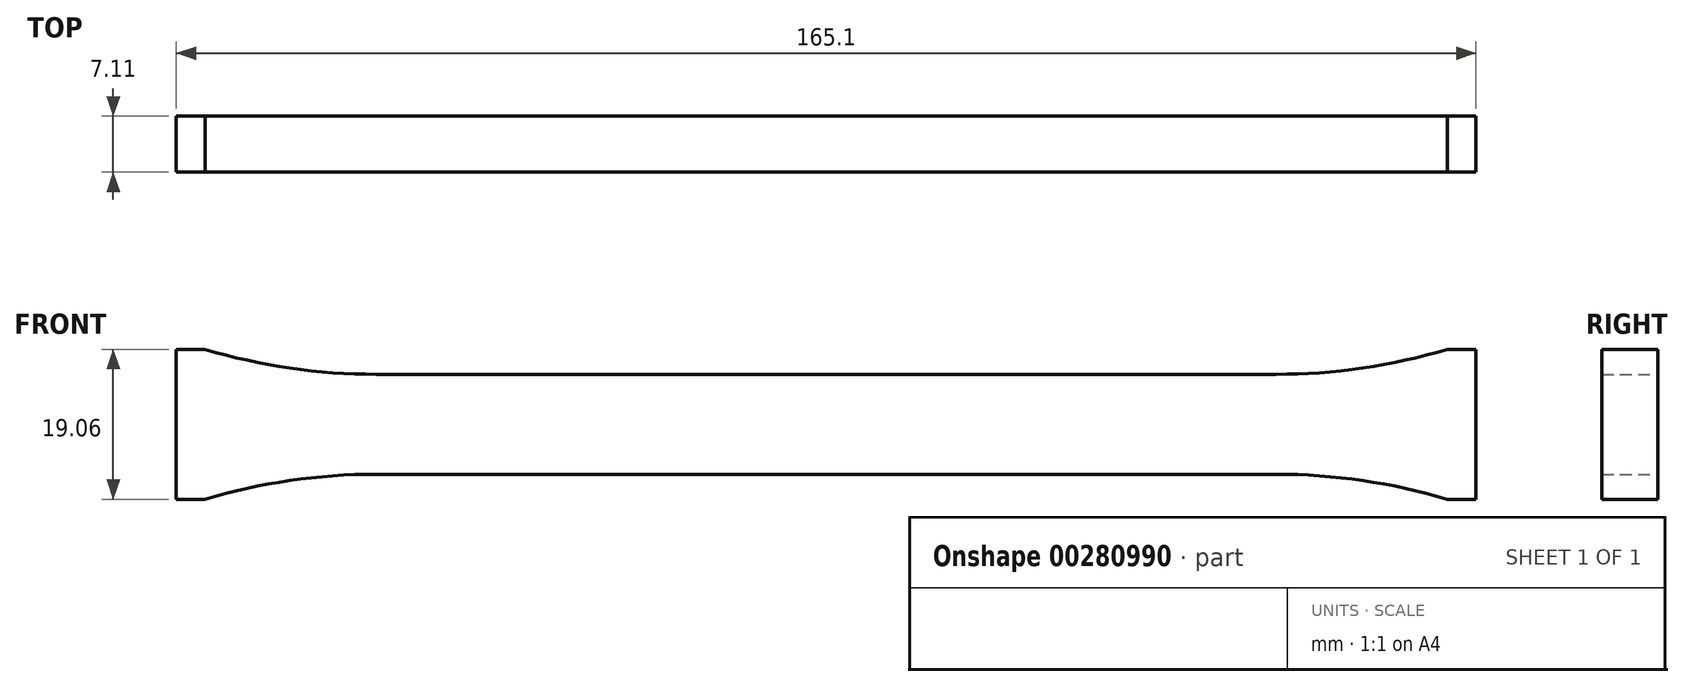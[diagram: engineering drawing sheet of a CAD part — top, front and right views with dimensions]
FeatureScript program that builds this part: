
annotation { "Feature Type Name" : "Feature", "Feature Type Description" : "" }
export const myFeature = defineFeature(function(context is Context, id is Id, definition is map)
    precondition{}
    {
        {
            var Q0;
            Q0=qCreatedBy(makeId("Front.planeOp"),FACE);
            var sketch = newSketch(context, id + "F0", { "sketchPlane" : qUnion([Q0])});
            skLineSegment(sketch, "E0", {"start": v(0, 6.35) * mm, "end": v(57.15, 6.35) * mm});
            skArc(sketch, "E1", {"start": v(57.15, 6.35) * mm, "mid": v(68.15, 7.15) * mm, "end": v(78.92, 9.53) * mm});
            skLineSegment(sketch, "E2", {"start": v(78.92, 9.53) * mm, "end": v(82.55, 9.53) * mm});
            skLineSegment(sketch, "E3", {"start": v(82.55, 9.52) * mm, "end": v(82.55, 0) * mm});
            skLineSegment(sketch, "E4.MirrorCS", {"start": v(82.55, -9.53) * mm, "end": v(82.55, 0) * mm});
            skLineSegment(sketch, "E5.MirrorCS", {"start": v(78.92, -9.53) * mm, "end": v(82.55, -9.53) * mm});
            skLineSegment(sketch, "E6.MirrorCS", {"start": v(0, -6.35) * mm, "end": v(57.15, -6.35) * mm});
            skArc(sketch, "E7.MirrorCS", {"start": v(57.15, -6.35) * mm, "mid": v(68.15, -7.15) * mm, "end": v(78.92, -9.53) * mm});
            skLineSegment(sketch, "E8.MirrorCS", {"start": v(-82.55, 9.52) * mm, "end": v(-82.55, 0) * mm});
            skLineSegment(sketch, "E9.MirrorCS", {"start": v(0, -6.35) * mm, "end": v(-57.15, -6.35) * mm});
            skArc(sketch, "E10.MirrorCS", {"start": v(-57.15, 6.35) * mm, "mid": v(-68.15, 7.15) * mm, "end": v(-78.92, 9.53) * mm});
            skLineSegment(sketch, "E11.MirrorCS", {"start": v(-78.92, 9.53) * mm, "end": v(-82.55, 9.53) * mm});
            skLineSegment(sketch, "E12.MirrorCS", {"start": v(-78.92, -9.52) * mm, "end": v(-82.55, -9.52) * mm});
            skLineSegment(sketch, "E13.MirrorCS", {"start": v(0, 6.35) * mm, "end": v(-57.15, 6.35) * mm});
            skLineSegment(sketch, "E14.MirrorCS", {"start": v(-82.55, -9.52) * mm, "end": v(-82.55, 0) * mm});
            skArc(sketch, "E15.MirrorCS", {"start": v(-57.15, -6.35) * mm, "mid": v(-68.15, -7.15) * mm, "end": v(-78.92, -9.53) * mm});
            skSolve(sketch);
        }
        {
            var Q0;
            Q0 = qSketchRegion(id + "F0", true);
            extrude(context, id + "F1", {"entities" : qUnion([Q0]), "depth" : 7.11 * mm});
        }
    });
